# Revit family: Plumbing-Faucet-Sloan-Valve-EAF-225_
name_source: partatom
category: Plumbing Fixtures
units: mm (PartAtom-declared; Revit-internal decimal feet)

## family parameters
Cut with Voids When Loaded = No
Host = Face
OmniClass Number = 23.45.55.14
OmniClass Title = Single Faucets
Part Type = Normal
Room Calculation Point = No
Round Connector Dimension = Use Diameter
Shared = No

## types (2) — shared parameters
Apparent Load = 0 VA
Assembly Code = D2010
CW Connection = Yes
CWFU = 1.5
Cold Water Connection Diameter = 0"
Connector Description = Electrical Connection
Current = 0 A
Default Elevation = 0"
Depth = 5 3/8"
Edition number = 1
HW Connection = Yes
HWFU = 1.5
Height = 5 3/8"
Hot Water Connection Diameter = 0"
Hot Water Connector Description = Hot Water Connection
Keynote = 15410
Manufacturer = Sloan Valve
Number of Poles = 1
Power Factor = 1
Product Material = Sloan Valve - Finish - Polished Chrome
Product data url = https://bimobject.com
URL = www.sloanvalve.com
Valve Pressure Drop = 0.00 psi
Vent Connection = No
Voltage = 6 V
Waste Connection = No
Water Flow = 1 GPM
Width = 2 1/8"
zero-valued in all types: WFU

## per-type parameters (varying)
| type | Description | Part Number |
| EAF-225-PLG-ISM-CP-0.5GPM-AER-IR-IQ-FCT | Plug Adapter Power Supply, Integrated Side Mixer, Polished Chrome Finish, 0.5 gpm, Aerated Spray, Infrared Sensor, Optima® HardwiredPowered Deck-Mounted Mid Body. | 3335075 |
| EAF-225-PLG-ISM-CP-1.0GPM-AER-IR-IQ-FCT | Plug Adapter Power Supply, Integrated Side Mixer, Polished Chrome Finish, 1.0 gpm, Aerated Spray, Infrared Sensor, Optima® HardwiredPowered Deck-Mounted Mid Body. | 3335130 |

note: column(s) folded — value = type name in every type: Model

## geometry (parser evidence)
native form markers: Sweep x4
no freeform markers — native parametric forms only
